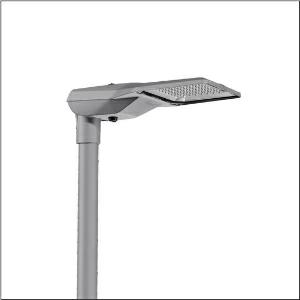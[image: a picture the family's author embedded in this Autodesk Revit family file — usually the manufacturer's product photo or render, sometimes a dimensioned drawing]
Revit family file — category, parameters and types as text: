
# Revit family: streetlight_sl_21_iq_midi___st1_0a_5xe3d61y08mb_8671
name_source: partatom
category: Lighting Fixtures
units: mm (PartAtom-declared; Revit-internal decimal feet)

## family parameters
Cut with Voids When Loaded = No
Host = Face
Light Source = No
Part Type = Normal
Room Calculation Point = No
Round Connector Dimension = Use Diameter
Shared = No

## types (1)
- --- (1 x LED, 15910 lm, 129.3 W, 2700K)
    Apparent Load = 129 VA
    CIE Flux Codes = 37 72 97 100 100
    Color Rendering = 70
    Color Temperature = 2700K
    Default Elevation = 1800 mm
    Description = Streetlight SL 21 iQ midi, mast luminaire, primary light control with lens, of PMMA, primary optical cover: cover, of toughened safety glass, transparent, light distribution: ST1.0a, light emission: direct distribution, primary light characteristic: asymmetric, installation type: post-top, side-entry, LED, High Power LED, rated luminous flux: 15.910lm, luminous efficacy: 123lm/W, light colour: 727, colour temperature: 2700K, control: pre-setting: logarithmic dimming characteristic, Street-Remote, Auto-Match, Temp-Guard, Lumen-Switch, Night-Set, Smart-Wire, Light-Fading, Desk-Remote (wireless, voltage-free reading and setting of iQ features in the workshop via application-optimized NFC function/RFID function), optimised constant luminous flux control (CLO 2.0), mains connection: 230..240V, AC, 50/60Hz, start of lifetime: 129W, end of service life: 142W, reduction: 56W, luminaire housing, of diecast aluminium, powder-coated, Siteco® metallic grey (DB 702S), corrosivity category C5 mid according to DIN EN ISO 12944, please order mast flange separately, inclination adjustable: 0°, 5°, 10°, 15°, sealing non-destructively replaceable, multi-level sealing system, length: 644mm, width: 335mm, height: 110mm, mast flange for spigot size: 42mm (side-entry): 5XC10008XM4, 60/48mm (side-entry/post-top): 5XC10108XM2, 76/60mm (side-entry/post-top): 5XC10108XM1, Smart Interface below and above, protection rating (complete): IP66, insulation class (complete): insulation class II (safety insulation), certification: CE, ENEC, ENEC+, VDE, impact resistance: IK09, permissible operating ambient temperature for outdoor applications: -40..+50°C, standard-compliant lighting for roads and squares, packaging unit: 1 piece

Light Distribution: ST1.0a
    Height = 111 mm
    Lamp = 1 x LED
    Lamp Light Flux = 15910 lm
    Lamp Power = 129.3 W
    Lamp count = 1
    Length = 644 mm
    Luminous efficacy = 123 lm/W
    Manufacturer = Siteco
    ModVariant = No
    Model = 5XE3D61Y08MB
    Number of Poles = 1
    OnlyDefault = Yes
    Power Factor = 1
    Product Name = Streetlight SL 21 iQ midi | ST1.0a
    Product group = mast luminaire | pylon top
    ProductGroupID = 6100
    Protection Class = Protection class II
    Protection Degree = IP 66
    RLX_Detail_Level = 1
    RLX_Emergency_Light_Flux = 0 lm
    RLX_Emergency_Type = 0
    RLX_Emergency_Type_DB = No
    RlxData = <blob elided: 90793 chars, md5=47b6ae6e>
    Socket = socket
    Standby Power = 0 W
    System Light Flux = 15910 lm
    System Power = 129 W
    Type Comments = factory setting: luminous flux: 100 % | dim-lin: 254 | 672 mA
    Type Image = l_1004304.jpg
    URL = http://relux.com
    VarID = @adj_083415
    Voltage = 0 V
    Weight = 0.00 kg
    Width = 336 mm

## geometry (parser evidence)
native form markers: Blend x4, Sweep x10
no freeform markers — native parametric forms only
